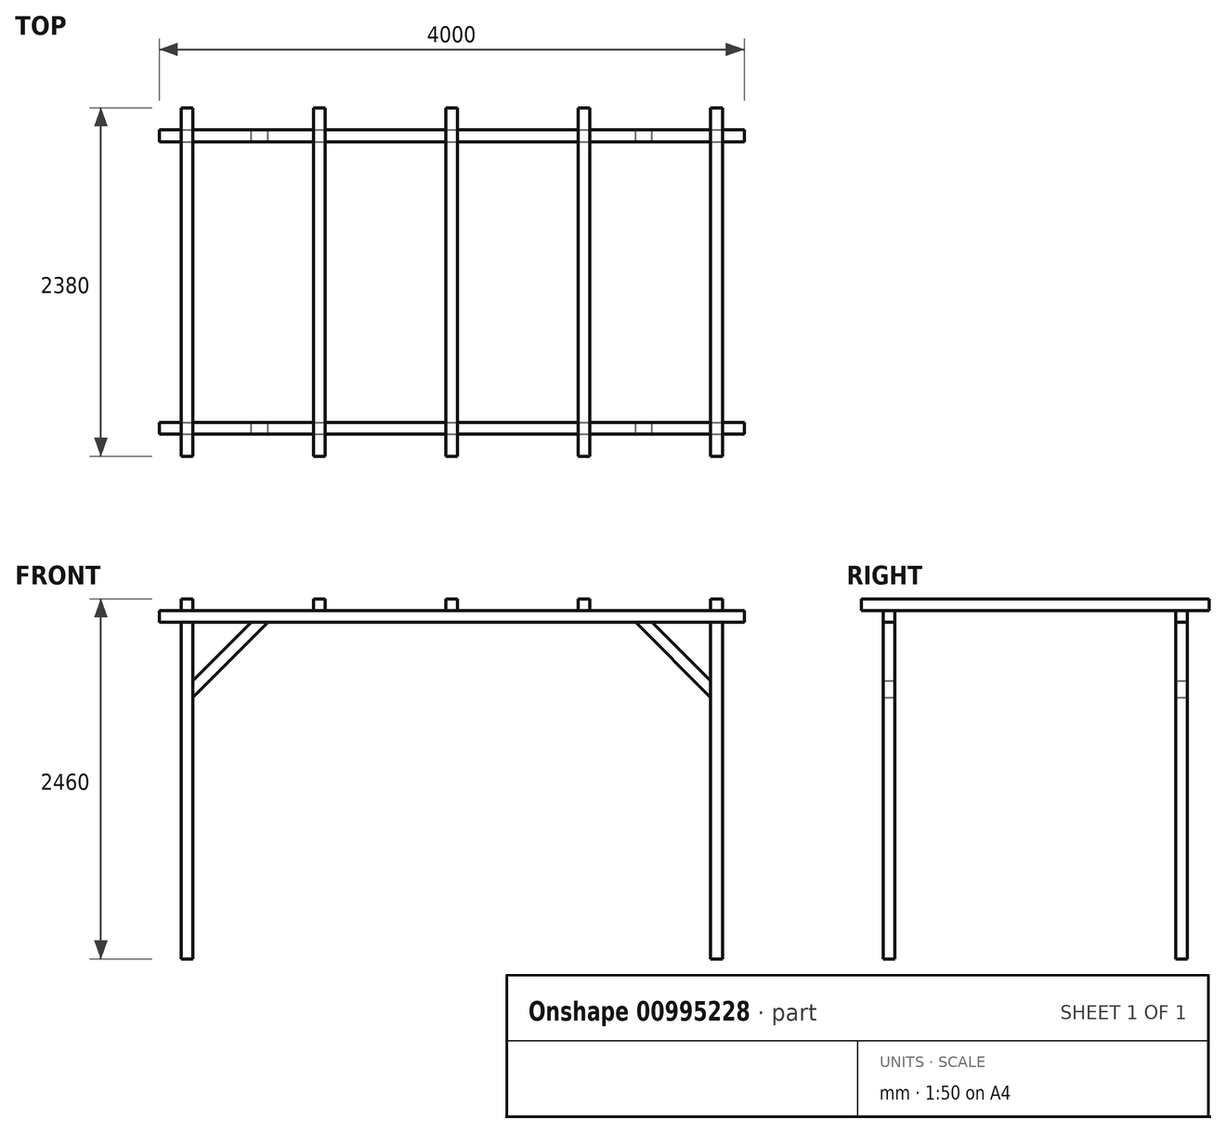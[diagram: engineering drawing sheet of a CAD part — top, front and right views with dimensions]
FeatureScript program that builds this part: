
annotation { "Feature Type Name" : "Feature", "Feature Type Description" : "" }
export const myFeature = defineFeature(function(context is Context, id is Id, definition is map)
    precondition{}
    {
        {
            var Q0;
            Q0=qCreatedBy(makeId("Front.planeOp"),FACE);
            var sketch = newSketch(context, id + "F0", { "sketchPlane" : qUnion([Q0])});
            skLineSegment(sketch, "E0.bottom", {"start": v(-2031.27, 1019.23) * mm, "end": v(-1951.27, 1019.23) * mm});
            skLineSegment(sketch, "E0.left", {"start": v(-2031.27, 1019.23) * mm, "end": v(-2031.27, -1280.77) * mm});
            skLineSegment(sketch, "E0.right", {"start": v(-1951.27, 1019.23) * mm, "end": v(-1951.27, -1280.77) * mm});
            skLineSegment(sketch, "E1.bottom", {"start": v(1588.73, 1019.23) * mm, "end": v(1668.73, 1019.23) * mm});
            skLineSegment(sketch, "E1.left", {"start": v(1588.73, 1019.23) * mm, "end": v(1588.73, -1280.77) * mm});
            skLineSegment(sketch, "E1.right", {"start": v(1668.73, 1019.23) * mm, "end": v(1668.73, -1280.77) * mm});
            skLineSegment(sketch, "E2.bottom", {"start": v(-2181.27, 1019.23) * mm, "end": v(1818.73, 1019.23) * mm});
            skLineSegment(sketch, "E2.top", {"start": v(-2181.27, 1099.23) * mm, "end": v(1818.73, 1099.23) * mm});
            skLineSegment(sketch, "E2.left", {"start": v(-2181.27, 1019.23) * mm, "end": v(-2181.27, 1099.23) * mm});
            skLineSegment(sketch, "E2.right", {"start": v(1818.73, 1019.23) * mm, "end": v(1818.73, 1099.23) * mm});
            skLineSegment(sketch, "E3", {"start": v(-2031.27, -1280.77) * mm, "end": v(-1951.27, -1280.77) * mm});
            skLineSegment(sketch, "E4", {"start": v(1588.73, -1280.77) * mm, "end": v(1668.73, -1280.77) * mm});
            skLineSegment(sketch, "E5", {"start": v(-1951.27, 619.23) * mm, "end": v(-1551.27, 1019.23) * mm});
            skLineSegment(sketch, "E6", {"start": v(-1951.27, 506.09) * mm, "end": v(-1438.13, 1019.23) * mm});
            skLineSegment(sketch, "E7", {"start": v(-1551.27, 1019.23) * mm, "end": v(-1438.13, 1019.23) * mm});
            skLineSegment(sketch, "E8", {"start": v(-1951.27, 619.23) * mm, "end": v(-1951.27, 506.09) * mm});
            skLineSegment(sketch, "E9", {"start": v(1188.73, 1019.23) * mm, "end": v(1588.73, 619.23) * mm});
            skLineSegment(sketch, "E10", {"start": v(1075.6, 1019.23) * mm, "end": v(1588.73, 506.09) * mm});
            skSolve(sketch);
        }
        {
            var Q0;
            {var subQ0=sQuery(id+"F0.wireOp",EDGE,"E0.left");Q0=makeQuery(id+"F0.imprint","IMPRINT",FACE,{"disambiguationData":[TD([[makeQuery(id+"F0.imprint","IMPRINT",EDGE,{"derivedFrom":subQ0}),1.0]])]});}
            extrude(context, id + "F1", {"entities" : qUnion([Q0]), "depth" : 80 * mm, "offsetDistance" : 25.4 * mm, "symmetric" : true});
        }
        {
            var Q0;
            {var subQ0=sQuery(id+"F0.wireOp",EDGE,"E1.left");Q0=makeQuery(id+"F0.imprint","IMPRINT",FACE,{"disambiguationData":[TD([[makeQuery(id+"F0.imprint","IMPRINT",EDGE,{"derivedFrom":subQ0}),1.0]])]});}
            extrude(context, id + "F2", {"entities" : qUnion([Q0]), "depth" : 80 * mm, "offsetDistance" : 25.4 * mm, "symmetric" : true});
        }
        {
            var Q0;
            Q0=makeQuery(id+"F0.imprint","IMPRINT",FACE,{"disambiguationData":[TD([[makeQuery(id+"F0.imprint","IMPRINT",EDGE,{"derivedFrom":sQuery(id+"F0.wireOp",EDGE,"E2.top")}),-1.0]])]});
            extrude(context, id + "F3", {"entities" : qUnion([Q0]), "depth" : 80 * mm, "offsetDistance" : 25.4 * mm, "symmetric" : true});
        }
        {
            var Q0;
            Q0=makeQuery(id+"F3.opExtrude","SWEPT_BODY",BODY,{"disambiguationData":[OSD([sQuery(id+"F0.wireOp",EDGE,"E2.bottom"),sQuery(id+"F0.wireOp",EDGE,"E2.top"),sQuery(id+"F0.wireOp",EDGE,"E2.left"),sQuery(id+"F0.wireOp",EDGE,"E2.right")])]});
            transform(context, id + "F4", {"entities" : qUnion([Q0]), "transformType" : TransformType.TRANSLATION_3D, "dx" : 0 * mm, "dy" : 2000 * mm, "dz" : 0 * mm, "makeCopy" : true});
        }
        {
            var Q0;
            Q0=makeQuery(id+"F2.opExtrude","SWEPT_BODY",BODY,{"disambiguationData":[OSD([sQuery(id+"F0.wireOp",EDGE,"E1.left"),sQuery(id+"F0.wireOp",EDGE,"E1.right"),sQuery(id+"F0.wireOp",EDGE,"E2.bottom"),sQuery(id+"F0.wireOp",EDGE,"E4")])]});
            transform(context, id + "F5", {"entities" : qUnion([Q0]), "transformType" : TransformType.TRANSLATION_3D, "dx" : 0 * mm, "dy" : 2000 * mm, "dz" : 0 * mm, "makeCopy" : true});
        }
        {
            var Q0;
            Q0=makeQuery(id+"F0.imprint","IMPRINT",FACE,{"disambiguationData":[TD([[makeQuery(id+"F0.imprint","IMPRINT",EDGE,{"derivedFrom":sQuery(id+"F0.wireOp",EDGE,"E5")}),-1.0]])]});
            var Q1;
            Q1=sQuery(id+"F0.wireOp",EDGE,"E5");
            var Q2;
            Q2=sQuery(id+"F0.wireOp",EDGE,"E8");
            var Q3;
            Q3=sQuery(id+"F0.wireOp",EDGE,"E6");
            var Q4;
            Q4=sQuery(id+"F0.wireOp",EDGE,"E7");
            extrude(context, id + "F6", {"entities" : qUnion([Q0]), "surfaceEntities" : qUnion([Q1, Q2, Q3, Q4]), "depth" : 80 * mm, "offsetDistance" : 25 * mm, "symmetric" : true});
        }
        {
            var Q0;
            Q0=makeQuery(id+"F1.opExtrude","SWEPT_BODY",BODY,{"disambiguationData":[OSD([sQuery(id+"F0.wireOp",EDGE,"E0.left"),sQuery(id+"F0.wireOp",EDGE,"E0.right"),sQuery(id+"F0.wireOp",EDGE,"E2.bottom"),sQuery(id+"F0.wireOp",EDGE,"E3")])]});
            transform(context, id + "F7", {"entities" : qUnion([Q0]), "transformType" : TransformType.TRANSLATION_3D, "dx" : 0 * mm, "dy" : 2000 * mm, "dz" : 0 * mm, "makeCopy" : true});
        }
        {
            var Q0;
            Q0=makeQuery(id+"F3.opExtrude","SWEPT_FACE",FACE,{"disambiguationData":[OSD([sQuery(id+"F0.wireOp",EDGE,"E2.top")])]});
            var Q1;
            Q1 = qBodyType(qCreatedBy(id + "F9" ,EDGE), BodyType.WIRE);
            cPlane(context, id + "F8", {"entities" : qUnion([Q0, Q1]), "cplaneType" : CPlaneType.OFFSET, "offset" : 0 * mm, "width" : 150 * mm, "height" : 150 * mm});
        }
        {
            var Q0;
            Q0=qCreatedBy(id+"F8.planeOp",FACE);
            var sketch = newSketch(context, id + "F9", { "sketchPlane" : qUnion([Q0])});
            skLineSegment(sketch, "E11.bottom", {"start": v(-2031.27, 2190) * mm, "end": v(-1951.27, 2190) * mm});
            skLineSegment(sketch, "E11.top", {"start": v(-2031.27, -190) * mm, "end": v(-1951.27, -190) * mm});
            skLineSegment(sketch, "E11.left", {"start": v(-2031.27, 2190) * mm, "end": v(-2031.27, -190) * mm});
            skLineSegment(sketch, "E11.right", {"start": v(-1951.27, 2190) * mm, "end": v(-1951.27, -190) * mm});
            skSolve(sketch);
        }
        {
            var Q0;
            Q0 = qSketchRegion(id + "F9", true);
            extrude(context, id + "F10", {"entities" : qUnion([Q0]), "depth" : 80 * mm, "offsetDistance" : 25 * mm});
        }
        {
            var Q0;
            Q0=makeQuery(id+"F10.opExtrude","SWEPT_BODY",BODY,{"disambiguationData":[OSD([sQuery(id+"F9.wireOp",EDGE,"E11.bottom"),sQuery(id+"F9.wireOp",EDGE,"E11.top"),sQuery(id+"F9.wireOp",EDGE,"E11.left"),sQuery(id+"F9.wireOp",EDGE,"E11.right")])]});
            transform(context, id + "F11", {"entities" : qUnion([Q0]), "transformType" : TransformType.TRANSLATION_3D, "dx" : 905 * mm, "dy" : 0 * mm, "dz" : 0 * mm, "makeCopy" : true});
        }
        {
            var Q0;
            Q0=makeQuery(id+"F11.opPattern","COPY",BODY,{"derivedFrom":makeQuery(id+"F10.opExtrude","SWEPT_BODY",BODY,{"disambiguationData":[OSD([sQuery(id+"F9.wireOp",EDGE,"E11.bottom"),sQuery(id+"F9.wireOp",EDGE,"E11.top"),sQuery(id+"F9.wireOp",EDGE,"E11.left"),sQuery(id+"F9.wireOp",EDGE,"E11.right")])]}),"instanceName":"1"});
            transform(context, id + "F12", {"entities" : qUnion([Q0]), "transformType" : TransformType.TRANSLATION_3D, "dx" : 905 * mm, "dy" : 0 * mm, "dz" : 0 * mm, "makeCopy" : true});
        }
        {
            var Q0;
            Q0=makeQuery(id+"F12.opPattern","COPY",BODY,{"derivedFrom":makeQuery(id+"F11.opPattern","COPY",BODY,{"derivedFrom":makeQuery(id+"F10.opExtrude","SWEPT_BODY",BODY,{"disambiguationData":[OSD([sQuery(id+"F9.wireOp",EDGE,"E11.bottom"),sQuery(id+"F9.wireOp",EDGE,"E11.top"),sQuery(id+"F9.wireOp",EDGE,"E11.left"),sQuery(id+"F9.wireOp",EDGE,"E11.right")])]}),"instanceName":"1"}),"instanceName":"1"});
            transform(context, id + "F13", {"entities" : qUnion([Q0]), "transformType" : TransformType.TRANSLATION_3D, "dx" : 905 * mm, "dy" : 0 * mm, "dz" : 0 * mm, "makeCopy" : true});
        }
        {
            var Q0;
            Q0=makeQuery(id+"F10.opExtrude","SWEPT_BODY",BODY,{"disambiguationData":[OSD([sQuery(id+"F9.wireOp",EDGE,"E11.bottom"),sQuery(id+"F9.wireOp",EDGE,"E11.top"),sQuery(id+"F9.wireOp",EDGE,"E11.left"),sQuery(id+"F9.wireOp",EDGE,"E11.right")])]});
            transform(context, id + "F14", {"entities" : qUnion([Q0]), "transformType" : TransformType.TRANSLATION_3D, "dx" : 3620 * mm, "dy" : 0 * mm, "dz" : 0 * mm, "makeCopy" : true});
        }
        {
            var Q0;
            {var subQ0=sQuery(id+"F0.wireOp",EDGE,"E9");Q0=makeQuery(id+"F0.imprint","IMPRINT",FACE,{"disambiguationData":[TD([[makeQuery(id+"F0.imprint","IMPRINT",EDGE,{"derivedFrom":subQ0}),-1.0]])]});}
            extrude(context, id + "F15", {"entities" : qUnion([Q0]), "depth" : 80 * mm, "offsetDistance" : 25 * mm, "symmetric" : true});
        }
        {
            var Q0;
            Q0=makeQuery(id+"F6.opExtrude","SWEPT_BODY",BODY,{"disambiguationData":[OSD([sQuery(id+"F0.wireOp",EDGE,"E5"),sQuery(id+"F0.wireOp",EDGE,"E6"),sQuery(id+"F0.wireOp",EDGE,"E7"),sQuery(id+"F0.wireOp",EDGE,"E8")])]});
            transform(context, id + "F16", {"entities" : qUnion([Q0]), "transformType" : TransformType.TRANSLATION_3D, "dx" : 0 * mm, "dy" : 2000 * mm, "dz" : 0 * mm, "makeCopy" : true});
        }
        {
            var Q0;
            Q0=makeQuery(id+"F15.opExtrude","SWEPT_BODY",BODY,{"disambiguationData":[OSD([sQuery(id+"F0.wireOp",EDGE,"E1.left"),sQuery(id+"F0.wireOp",EDGE,"E2.bottom"),sQuery(id+"F0.wireOp",EDGE,"E9"),sQuery(id+"F0.wireOp",EDGE,"E10")])]});
            transform(context, id + "F17", {"entities" : qUnion([Q0]), "transformType" : TransformType.TRANSLATION_3D, "dx" : 0 * mm, "dy" : 2000 * mm, "dz" : 0 * mm, "makeCopy" : true});
        }
    });
